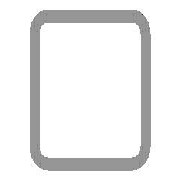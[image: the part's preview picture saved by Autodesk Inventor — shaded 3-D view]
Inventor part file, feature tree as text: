
AUTODESK INVENTOR PART (.ipt)
format: ipt  version: 2025 (Build 290162010, 162A)  size: 132,608 bytes
history: native  units: mm (DEFAULTED — no unit token found)
features: other x4, sketch x1, plane x1
ambient origin geometry x8: Origin, YZ Plane, XZ Plane, XY Plane, X Axis, Y Axis, Z Axis, Center Point
bodies: Solid1 (feature_tree), Body (feature_tree)
feature tree (6):
  parser-record x1  (decoder bookkeeping rows leaked as tree rows — omitted from the tree; the rows remain in map.json)
  other  "Driven Length"
  other  "Start Plane"
  other  "End Plane"
  sketch  "Sketch3"  dims[d3=2040.0mm d4=0.0mm d7=4.0mm d9=40.0mm d11=40.0mm d12=2.0mm d13=-0.0mm d14=2040.0mm d15=20.0mm d16=20.0mm d17=90.0deg d18=2040.0mm]
  plane  "Work Plane3"
